# Revit family: HS 821-síto_standard-PN16-DN040-RFA_2019
name_source: partatom
category: Pipe Accessories
units: mm (PartAtom-declared; Revit-internal decimal feet)

## family parameters
Always vertical = Yes
Cut with Voids When Loaded = No
Part Type = Breaks Into
Round Connector Dimension = Use Diameter
Shared = No
Work Plane-Based = No

## types (40) — shared parameters
CAT0 = Yes
Description = Filtr přírubový; síto standardní; 821A-PN16; 821D-PN25; 821F-PN40
L2D = 130 mm
L2D_Min = 3048 mm
Manufacturer = Hydronix
QmdConnectorList = 301;D;302;D
Type Comments = Filtr přírubový; síto standardní; A-PN16 (-10~300°C); D-PN25 (-10~350°C); F-PN40 (-10~400°C)
URL = www.hydronix.cz
W2D = 15 mm  [stored 0.0492126 ft]
magiPartTypeId = 307
magiProductFamilyId = 79214ac3aaa945e397802f559f5c1e

## per-type parameters (varying)
| type | BD | C | C1 | CC | D | DM | DM1 | FD | HH2 | L2 | L4 | LM | LM1 | MC Product Code | S | X1 | X2 | ZB | ZB1 | ZB__ve | magiProductId |
| 821A-DN015-PN16-síto_standard | 13 mm  [stored 0.0426509 ft] | 13 mm  [stored 0.0426509 ft] | 11 mm | 2 mm  [stored 0.00656168 ft] | 15 mm | 41 mm | 28 mm | 95 mm | 81 mm | 65 mm | 33 mm | 104 mm | 10 mm  [stored 0.0328084 ft] | 200 115 (821A; DN015; PN16; kvs6,3; oko síta 1,00mm) | 46 mm | 18 mm  [stored 0.0590551 ft] | 47 mm | 16 mm  [stored 0.0524934 ft] | 19 mm | -16 mm | a71bcfe8b393460598b23e8ddf7dc5 |
| 821A-DN020-PN16-síto_standard | 16 mm  [stored 0.0524934 ft] | 15 mm  [stored 0.0492126 ft] | 12 mm  [stored 0.0393701 ft] | 3 mm  [stored 0.00984252 ft] | 20 mm | 50 mm | 34 mm | 105 mm | 90 mm | 75 mm | 38 mm | 120 mm | 12 mm  [stored 0.0393701 ft] | 200 120 (821A; DN020; PN16; kvs11,2; oko síta 1,00mm) | 56 mm | 21 mm  [stored 0.0688976 ft] | 52 mm | 18 mm  [stored 0.0590551 ft] | 23 mm | -18 mm | 41cd6c7a12924f4991217528336076 |
| 821A-DN025-PN16-síto_standard | 18 mm  [stored 0.0590551 ft] | 16 mm  [stored 0.0524934 ft] | 13 mm  [stored 0.0426509 ft] | 3 mm  [stored 0.00984252 ft] | 25 mm | 59 mm | 43 mm | 115 mm | 102 mm | 80 mm | 40 mm | 128 mm | 13 mm  [stored 0.0426509 ft] | 200 125 (821A; DN025; PN16; kvs14,7; oko síta 1,00mm) | 65 mm | 22 mm | 59 mm | 19 mm | 26 mm | -19 mm | be378b463ed14c3abf4c9b3ae8cf3a |
| 821A-DN032-PN16-síto_standard | 22 mm | 18 mm  [stored 0.0590551 ft] | 15 mm  [stored 0.0492126 ft] | 3 mm  [stored 0.00984252 ft] | 32 mm | 68 mm | 50 mm | 140 mm | 119 mm | 90 mm | 45 mm | 144 mm | 14 mm  [stored 0.0459318 ft] | 200 132 (821A; DN032; PN16; kvs23,7; oko síta 1,00mm) | 76 mm | 25 mm | 69 mm | 23 mm | 31 mm | -23 mm  [stored -0.0754593 ft] | 227a0d18b21540afabe8b6067d35fa |
| 821A-DN040-PN16-síto_standard | 24 mm | 20 mm  [stored 0.0656168 ft] | 17 mm | 3 mm  [stored 0.00984252 ft] | 40 mm | 76 mm | 60 mm | 150 mm | 131 mm | 100 mm | 50 mm | 160 mm | 16 mm  [stored 0.0524934 ft] | 200 140 (821A; DN040; PN16; kvs37,7; oko síta 1,00mm) | 84 mm | 28 mm | 76 mm | 25 mm | 34 mm | -25 mm | d106917c74724141a10440112d0102 |
| 821A-DN050-PN16-síto_standard | 28 mm | 23 mm | 19 mm | 4 mm  [stored 0.0131234 ft] | 50 mm | 89 mm | 74 mm | 165 mm | 137 mm | 115 mm | 58 mm | 184 mm | 18 mm  [stored 0.0590551 ft] | 200 150 (821A; DN050 PN16; kvs57,9; oko síta 1,00mm) | 99 mm | 32 mm | 79 mm | 27 mm | 40 mm | -27 mm | 8255d456a09e4f6486734f5dd9171b |
| 821A-DN065-PN16-síto_standard | 33 mm | 29 mm | 24 mm | 5 mm  [stored 0.0164042 ft] | 65 mm | 106 mm | 94 mm | 185 mm | 151 mm | 145 mm | 73 mm | 232 mm | 23 mm | 200 165 (821A; DN065; PN16; kvs101,5; oko síta 1,25mm) | 118 mm | 41 mm | 87 mm | 30 mm | 48 mm | -30 mm | 235b1b3e4c0843779a4d5e3716d40a |
| 821A-DN080-PN16-síto_standard | 37 mm | 31 mm | 26 mm | 5 mm  [stored 0.0164042 ft] | 80 mm | 119 mm | 107 mm | 200 mm | 181 mm | 155 mm | 78 mm | 248 mm | 25 mm | 200 180 (821A; DN080; PN16; kvs147,4; oko síta 1,25mm) | 132 mm | 43 mm | 105 mm | 32 mm | 53 mm | -32 mm  [stored -0.104987 ft] | a067f7c5236348ed8c820d16df7214 |
| 821A-DN100-PN16-síto_standard | 44 mm | 35 mm | 29 mm | 6 mm  [stored 0.019685 ft] | 100 mm | 140 mm | 131 mm | 220 mm | 199 mm | 175 mm | 88 mm | 280 mm | 28 mm | 200 190 (821A; DN100; PN16; kvs209,6; oko síta 1,60mm) | 156 mm | 49 mm | 115 mm | 35 mm | 63 mm | -35 mm  [stored -0.114829 ft] | c49a648c2747461285837d643703cd |
| 821A-DN125-PN16-síto_standard | 52 mm | 40 mm | 33 mm | 7 mm  [stored 0.0229659 ft] | 125 mm | 166 mm | 165 mm | 250 mm | 228 mm | 200 mm | 100 mm | 320 mm | 32 mm | 200 191 (821A; DN125; PN16; kvs326,2; oko síta 1,60mm) | 184 mm | 56 mm | 132 mm | 40 mm | 75 mm | -40 mm | bf68e728a163493cbd2a663b26ebdc |
| 821A-DN150-PN16-síto_standard | 60 mm | 48 mm | 40 mm | 8 mm  [stored 0.0262467 ft] | 150 mm | 190 mm | 192 mm | 285 mm | 270 mm | 240 mm | 120 mm | 384 mm | 38 mm | 200 192 (821A; DN150; PN16; kvs403; oko síta 1,60mm) | 211 mm | 67 mm | 156 mm | 45 mm | 85 mm | -45 mm | 2de770284b654863ae6bc865769dc5 |
| 821A-DN200-PN16-síto_standard | 75 mm | 60 mm | 50 mm | 10 mm  [stored 0.0328084 ft] | 200 mm | 239 mm | 252 mm | 340 mm | 326 mm | 300 mm | 150 mm | 480 mm | 48 mm | 200 193 (821A; DN200; PN16; kvs707; oko síta 1,60mm) | 266 mm | 84 mm | 188 mm | 53 mm | 108 mm | -53 mm  [stored -0.173885 ft] | 8e5693371ab64aabb29a7f08c76e15 |
| 821A-DN250-PN16-síto_standard | 90 mm | 73 mm | 61 mm | 12 mm  [stored 0.0393701 ft] | 250 mm | 287 mm | 310 mm | 405 mm | 443 mm | 365 mm | 183 mm | 584 mm | 58 mm | 200 194 (821A; DN250; PN16; kvs1234; oko síta 1,60mm) | 319 mm | 102 mm | 256 mm | 63 mm | 129 mm | -63 mm | 05e37ed948c34047acdd4c42556504 |
| 821A-DN300-PN16-síto_standard | 105 mm | 85 mm | 71 mm | 14 mm  [stored 0.0459318 ft] | 300 mm | 333 mm | 370 mm | 460 mm | 565 mm | 425 mm | 213 mm | 680 mm | 68 mm | 200 195 (821A; DN300; PN16; kvs1916; oko síta 1,60mm) | 370 mm | 119 mm | 326 mm | 71 mm | 150 mm | -71 mm  [stored -0.23294 ft] | 9ad0af747269428da925480d83ce80 |
| 821A-DN350-PN16-síto_standard | 122 mm | 98 mm | 81 mm | 17 mm | 350 mm | 386 mm | 438 mm | 520 mm | 618 mm | 490 mm | 245 mm | 784 mm | 78 mm | 200 196 (821A; DN350; PN16; kvs2621; oko síta 1,60mm) | 429 mm | 137 mm | 357 mm | 80 mm | 174 mm | -80 mm  [stored -0.262467 ft] | eebc71459bb3451bb4355e7951370a |
| 821A-DN400-PN16-síto_standard | 136 mm | 110 mm | 91 mm | 19 mm | 400 mm | 432 mm | 498 mm | 580 mm | 679 mm | 550 mm | 275 mm | 880 mm | 88 mm | 200 197 (821A; DN400; PN16; kvs3460; oko síta 1,60mm) | 480 mm | 154 mm | 392 mm | 89 mm | 194 mm | -89 mm  [stored -0.291995 ft] | d2f677cb196647e385b2590e7d8abe |
| 821D-DN015-PN25-síto_standard | 13 mm  [stored 0.0426509 ft] | 13 mm  [stored 0.0426509 ft] | 11 mm | 2 mm  [stored 0.00656168 ft] | 15 mm | 41 mm | 28 mm | 95 mm | 81 mm | 65 mm | 33 mm | 104 mm | 10 mm  [stored 0.0328084 ft] | 200 215 (821D; DN015; PN25; kvs6,3; oko síta 1,00mm) | 46 mm | 18 mm  [stored 0.0590551 ft] | 47 mm | 16 mm  [stored 0.0524934 ft] | 19 mm | -16 mm | 27ddcbf555414f8ca1fde329bf9087 |
| 821D-DN020-PN25-síto_standard | 16 mm  [stored 0.0524934 ft] | 15 mm  [stored 0.0492126 ft] | 12 mm  [stored 0.0393701 ft] | 3 mm  [stored 0.00984252 ft] | 20 mm | 50 mm | 34 mm | 105 mm | 90 mm | 75 mm | 38 mm | 120 mm | 12 mm  [stored 0.0393701 ft] | 200 220 (821D; DN020; PN25; kvs11,2; oko síta 1,00mm) | 56 mm | 21 mm  [stored 0.0688976 ft] | 52 mm | 18 mm  [stored 0.0590551 ft] | 23 mm | -18 mm | 270e0f14012f47189cd0235c18faee |
| 821D-DN025-PN25-síto_standard | 18 mm  [stored 0.0590551 ft] | 16 mm  [stored 0.0524934 ft] | 13 mm  [stored 0.0426509 ft] | 3 mm  [stored 0.00984252 ft] | 25 mm | 59 mm | 43 mm | 115 mm | 102 mm | 80 mm | 40 mm | 128 mm | 13 mm  [stored 0.0426509 ft] | 200 225 (821D; DN025; PN25; kvs14,7; oko síta 1,00mm) | 65 mm | 22 mm | 59 mm | 19 mm | 26 mm | -19 mm | b9a7fb4aa36643878c637d8e1ab992 |
| 821D-DN032-PN25-síto_standard | 22 mm | 18 mm  [stored 0.0590551 ft] | 15 mm  [stored 0.0492126 ft] | 3 mm  [stored 0.00984252 ft] | 32 mm | 68 mm | 50 mm | 140 mm | 119 mm | 90 mm | 45 mm | 144 mm | 14 mm  [stored 0.0459318 ft] | 200 232 (821D; DN032; PN25; kvs23,7; oko síta 1,00mm) | 76 mm | 25 mm | 69 mm | 23 mm | 31 mm | -23 mm  [stored -0.0754593 ft] | 6be9a55c4e68400f94eec7e804204c |
| 821D-DN040-PN25-síto_standard | 24 mm | 20 mm  [stored 0.0656168 ft] | 17 mm | 3 mm  [stored 0.00984252 ft] | 40 mm | 76 mm | 60 mm | 150 mm | 131 mm | 100 mm | 50 mm | 160 mm | 16 mm  [stored 0.0524934 ft] | 200 240 (821D; DN040; PN25; kvs37,7; oko síta 1,00mm) | 84 mm | 28 mm | 76 mm | 25 mm | 34 mm | -25 mm | c54511bd7f584ec2984291479612cb |
| 821D-DN050-PN25-síto_standard | 28 mm | 23 mm | 19 mm | 4 mm  [stored 0.0131234 ft] | 50 mm | 89 mm | 74 mm | 165 mm | 137 mm | 115 mm | 58 mm | 184 mm | 18 mm  [stored 0.0590551 ft] | 200 250 (821D; DN050; PN25; kvs57,9; oko síta 1,00mm) | 99 mm | 32 mm | 79 mm | 27 mm | 40 mm | -27 mm | 5483b1f596b04cd39b23a14a22c90e |
| 821D-DN065-PN25-síto_standard | 33 mm | 29 mm | 24 mm | 5 mm  [stored 0.0164042 ft] | 65 mm | 106 mm | 94 mm | 185 mm | 151 mm | 145 mm | 73 mm | 232 mm | 23 mm | 200 265 (821D; DN065; PN25; kvs101,5; oko síta 1,25mm) | 118 mm | 41 mm | 87 mm | 30 mm | 48 mm | -30 mm | 767b0f8318e94750bc7a9930ed5b30 |
| 821D-DN080-PN25-síto_standard | 37 mm | 31 mm | 26 mm | 5 mm  [stored 0.0164042 ft] | 80 mm | 119 mm | 107 mm | 200 mm | 181 mm | 155 mm | 78 mm | 248 mm | 25 mm | 200 280 (821D; DN080; PN25; kvs147,4; oko síta 1,25mm) | 132 mm | 43 mm | 105 mm | 32 mm | 53 mm | -32 mm  [stored -0.104987 ft] | e21040fa3cc2404b858198f6b73709 |
| 821D-DN100-PN25-síto_standard | 44 mm | 35 mm | 29 mm | 6 mm  [stored 0.019685 ft] | 100 mm | 140 mm | 131 mm | 235 mm | 199 mm | 175 mm | 88 mm | 280 mm | 28 mm | 200 290 (821D; DN100; PN25; kvs209,6; oko síta 1,60mm) | 156 mm | 49 mm | 115 mm | 37 mm | 63 mm | -37 mm | 175ca87a506b40b3bc6b82f12f33cf |
| 821D-DN125-PN25-síto_standard | 52 mm | 40 mm | 33 mm | 7 mm  [stored 0.0229659 ft] | 125 mm | 166 mm | 165 mm | 270 mm | 228 mm | 200 mm | 100 mm | 320 mm | 32 mm | 200 291 (821D; DN125; PN25; kvs326,2; oko síta 1,60mm) | 184 mm | 56 mm | 132 mm | 43 mm | 75 mm | -43 mm | 77cc98d60da24855999a22dff726b2 |
| 821D-DN150-PN25-síto_standard | 60 mm | 48 mm | 40 mm | 8 mm  [stored 0.0262467 ft] | 150 mm | 190 mm | 192 mm | 300 mm | 270 mm | 240 mm | 120 mm | 384 mm | 38 mm | 200 292 (821D; DN150; PN25; kvs403; oko síta 1,60mm) | 211 mm | 67 mm | 156 mm | 47 mm | 85 mm | -47 mm  [stored -0.154199 ft] | 9cf8acfcd15547d68e83172d3abcbe |
| 821D-DN200-PN25-síto_standard | 78 mm | 60 mm | 50 mm | 10 mm  [stored 0.0328084 ft] | 200 mm | 247 mm | 252 mm | 360 mm | 326 mm | 300 mm | 150 mm | 480 mm | 48 mm | 200 293 (821D; DN200; PN25; kvs707; oko síta 1,60mm) | 274 mm | 84 mm | 188 mm | 56 mm | 111 mm | -56 mm  [stored -0.183727 ft] | 16973f3c9ea14389ba8602495a6b64 |
| 821F-DN015-PN40-síto_standard | 13 mm  [stored 0.0426509 ft] | 13 mm  [stored 0.0426509 ft] | 11 mm | 2 mm  [stored 0.00656168 ft] | 15 mm | 41 mm | 28 mm | 95 mm | 81 mm | 65 mm | 33 mm | 104 mm | 10 mm  [stored 0.0328084 ft] | 240 615 (821F; DN015; PN40; kvs6,3; oko síta 1,00mm) | 45 mm | 18 mm  [stored 0.0590551 ft] | 47 mm | 16 mm  [stored 0.0524934 ft] | 18 mm  [stored 0.0590551 ft] | -16 mm | 4c7eaf3c4c0340888b3e684d8a8616 |
| 821F-DN020-PN40-síto_standard | 16 mm  [stored 0.0524934 ft] | 15 mm  [stored 0.0492126 ft] | 12 mm  [stored 0.0393701 ft] | 3 mm  [stored 0.00984252 ft] | 20 mm | 52 mm | 34 mm | 105 mm | 90 mm | 75 mm | 38 mm | 120 mm | 12 mm  [stored 0.0393701 ft] | 240 620 (821F; DN020; PN40; kvs11,2; oko síta 1,00mm) | 58 mm | 21 mm  [stored 0.0688976 ft] | 52 mm | 18 mm  [stored 0.0590551 ft] | 23 mm | -18 mm | aaac5f1ec96b44d6ba96ac2293d66d |
| 821F-DN025-PN40-síto_standard | 19 mm | 16 mm  [stored 0.0524934 ft] | 13 mm  [stored 0.0426509 ft] | 3 mm  [stored 0.00984252 ft] | 25 mm | 61 mm | 43 mm | 115 mm | 102 mm | 80 mm | 40 mm | 128 mm | 13 mm  [stored 0.0426509 ft] | 240 625 (821F; DN025; PN40; kvs14,7; oko síta 1,00mm) | 68 mm | 22 mm | 59 mm | 19 mm | 28 mm | -19 mm | 504768023968471481789485b54c7e |
| 821F-DN032-PN40-síto_standard | 22 mm | 18 mm  [stored 0.0590551 ft] | 15 mm  [stored 0.0492126 ft] | 3 mm  [stored 0.00984252 ft] | 32 mm | 70 mm | 50 mm | 140 mm | 119 mm | 90 mm | 45 mm | 144 mm | 14 mm  [stored 0.0459318 ft] | 240 632 (821F; DN032; PN40; kvs23,7; oko síta 1,00mm) | 78 mm | 25 mm | 69 mm | 23 mm | 32 mm | -23 mm  [stored -0.0754593 ft] | 165e7f39cf744f329bdf1c400dad12 |
| 821F-DN040-PN40-síto_standard | 25 mm | 20 mm  [stored 0.0656168 ft] | 17 mm | 3 mm  [stored 0.00984252 ft] | 40 mm | 79 mm | 60 mm | 150 mm | 131 mm | 100 mm | 50 mm | 160 mm | 16 mm  [stored 0.0524934 ft] | 240 640 (821F; DN040; PN40; kvs37,7; oko síta 1,00mm) | 88 mm | 28 mm | 76 mm | 25 mm | 36 mm | -25 mm | b8903f952089408fbf3a5a632bab1f |
| 821F-DN050-PN40-síto_standard | 29 mm | 23 mm | 19 mm | 4 mm  [stored 0.0131234 ft] | 50 mm | 92 mm | 74 mm | 165 mm | 137 mm | 115 mm | 58 mm | 184 mm | 18 mm  [stored 0.0590551 ft] | 240 650 (821F; DN050; PN40; kvs57,9; oko síta 1,00mm) | 102 mm | 32 mm | 79 mm | 27 mm | 41 mm | -27 mm | c451f97266fe48da8f879cb6a2bd44 |
| 821F-DN065-PN40-síto_standard | 35 mm | 29 mm | 24 mm | 5 mm  [stored 0.0164042 ft] | 65 mm | 110 mm | 94 mm | 185 mm | 151 mm | 145 mm | 73 mm | 232 mm | 23 mm | 240 665 (821F; DN065; PN40; kvs101,5; oko síta 1,25mm) | 122 mm | 41 mm | 87 mm | 30 mm | 49 mm | -30 mm | dc9821e3f9b34e128f6a8c6b34c198 |
| 821F-DN080-PN40-síto_standard | 39 mm | 31 mm | 26 mm | 5 mm  [stored 0.0164042 ft] | 80 mm | 124 mm | 107 mm | 200 mm | 181 mm | 155 mm | 78 mm | 248 mm | 25 mm | 240 680 (821F; DN080; PN40; kvs147,4; oko síta 1,25mm) | 138 mm | 43 mm | 105 mm | 32 mm | 56 mm | -32 mm  [stored -0.104987 ft] | 689aa1e260f84cf4994f027a1d86b5 |
| 821F-DN100-PN40-síto_standard | 46 mm | 35 mm | 29 mm | 6 mm  [stored 0.019685 ft] | 100 mm | 146 mm | 131 mm | 235 mm | 199 mm | 175 mm | 88 mm | 280 mm | 28 mm | 240 690 (821F; DN100; PN40; kvs209,6; oko síta 1,6mm) | 162 mm | 49 mm | 115 mm | 37 mm | 66 mm | -37 mm | 8a45d4e8e2ab425f8c432f21d684f3 |
| 821F-DN125-PN40-síto_standard | 53 mm | 40 mm | 33 mm | 7 mm  [stored 0.0229659 ft] | 125 mm | 169 mm | 165 mm | 270 mm | 228 mm | 200 mm | 100 mm | 320 mm | 32 mm | 240 691 (821F; DN125; PN40; kvs326,2; oko síta 1,6mm) | 188 mm | 56 mm | 132 mm | 43 mm | 76 mm | -43 mm | cf073904c006406b8645afa67ea2fc |
| 821F-DN150-PN40-síto_standard | 62 mm | 48 mm | 40 mm | 8 mm  [stored 0.0262467 ft] | 150 mm | 196 mm | 192 mm | 300 mm | 270 mm | 240 mm | 120 mm | 384 mm | 38 mm | 240 692 (821F; DN150; PN40; kvs403; oko síta 1,6mm) | 218 mm | 67 mm | 156 mm | 47 mm | 88 mm | -47 mm  [stored -0.154199 ft] | 0153b9ddabe14992a630484929fdbc |
| 821F-DN200-PN40-síto_standard | 81 mm | 60 mm | 50 mm | 10 mm  [stored 0.0328084 ft] | 200 mm | 257 mm | 252 mm | 360 mm | 326 mm | 300 mm | 150 mm | 480 mm | 48 mm | 240 693 (821F; DN200; PN40; kvs707; oko síta 1,6mm) | 285 mm | 84 mm | 188 mm | 56 mm | 115 mm | -56 mm  [stored -0.183727 ft] | 7fb3fc01dd8d42428c203e3f8dd4d5 |

note: [stored X ft] marks values corroborated as IEEE doubles in the binary element streams (Revit-internal decimal feet)

## geometry (parser evidence)
native form markers: Sweep x1
no freeform markers — native parametric forms only
